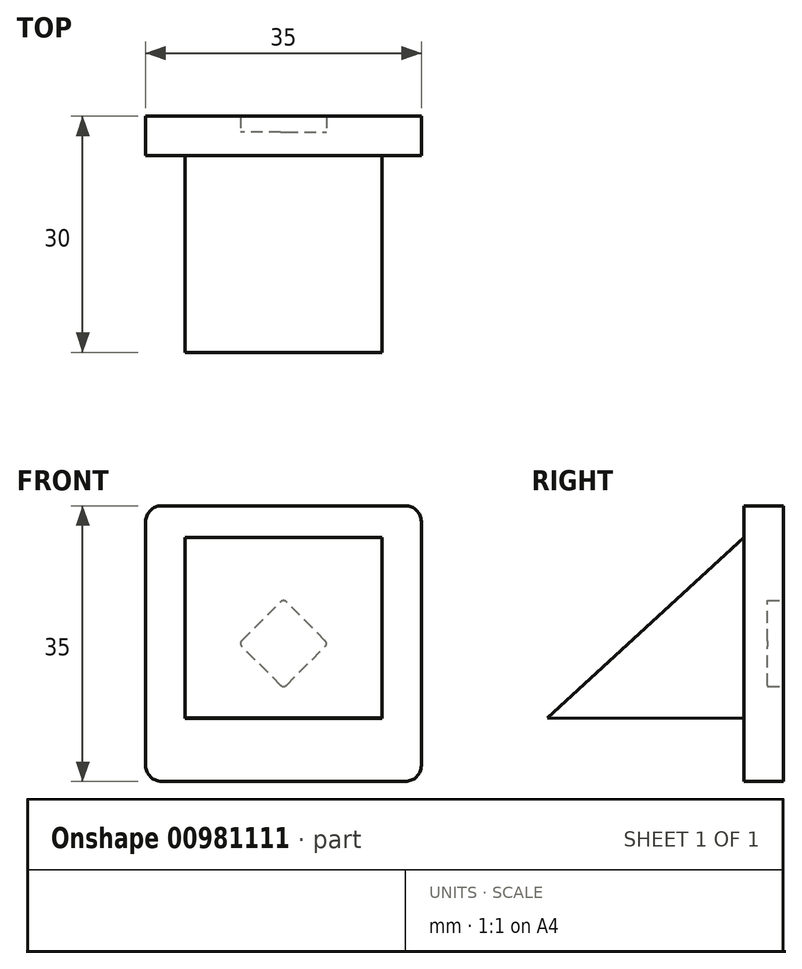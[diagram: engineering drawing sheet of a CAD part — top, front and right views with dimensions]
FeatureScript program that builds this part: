
annotation { "Feature Type Name" : "Feature", "Feature Type Description" : "" }
export const myFeature = defineFeature(function(context is Context, id is Id, definition is map)
    precondition{}
    {
        {
            var Q0;
            Q0=qCreatedBy(makeId("Front.planeOp"),FACE);
            var sketch = newSketch(context, id + "F0", { "sketchPlane" : qUnion([Q0])});
            skLineSegment(sketch, "E0.bottom", {"start": v(-17.5, 35) * mm, "end": v(17.5, 35) * mm});
            skLineSegment(sketch, "E0.top", {"start": v(-17.5, 0) * mm, "end": v(17.5, 0) * mm});
            skLineSegment(sketch, "E0.left", {"start": v(-17.5, 35) * mm, "end": v(-17.5, 0) * mm});
            skLineSegment(sketch, "E0.right", {"start": v(17.5, 35) * mm, "end": v(17.5, 0) * mm});
            skLineSegment(sketch, "E1.bottom", {"start": v(0, 11.84) * mm, "end": v(-5.66, 17.5) * mm});
            skLineSegment(sketch, "E1.top", {"start": v(5.66, 17.5) * mm, "end": v(0, 23.16) * mm});
            skLineSegment(sketch, "E1.left", {"start": v(0, 11.84) * mm, "end": v(5.66, 17.5) * mm});
            skLineSegment(sketch, "E1.right", {"start": v(-5.66, 17.5) * mm, "end": v(0, 23.16) * mm});
            skPoint(sketch, "E1.middle", {"position": v(0, 17.5) * mm});
            skLineSegment(sketch, "E2", {"start": v(-17.5, 17.5) * mm, "end": v(-5.66, 17.5) * mm, "construction": true});
            skArc(sketch, "E3", {"start": v(17.5, 3) * mm, "mid": v(0, 4) * mm, "end": v(-17.5, 3) * mm});
            skLineSegment(sketch, "E4", {"start": v(-17.5, 3) * mm, "end": v(17.5, 3) * mm, "construction": true});
            skSolve(sketch);
        }
        {
            var Q0;
            {var subQ0=sQuery(id+"F0.wireOp",EDGE,"E0.top");Q0=makeQuery(id+"F0.imprint","IMPRINT",FACE,{"disambiguationData":[TD([[makeQuery(id+"F0.imprint","IMPRINT",EDGE,{"derivedFrom":subQ0}),1.0]])]});}
            var Q1;
            {var subQ1=sQuery(id+"F0.wireOp",EDGE,"E0.bottom");Q1=makeQuery(id+"F0.imprint","IMPRINT",FACE,{"disambiguationData":[TD([[makeQuery(id+"F0.imprint","IMPRINT",EDGE,{"derivedFrom":subQ1}),-1.0]])]});}
            var Q2;
            Q2=makeQuery(id+"F0.imprint","IMPRINT",FACE,{"disambiguationData":[TD([[makeQuery(id+"F0.imprint","IMPRINT",EDGE,{"derivedFrom":sQuery(id+"F0.wireOp",EDGE,"E1.bottom")}),-1.0]])]});
            extrude(context, id + "F1", {"entities" : qUnion([Q0, Q1, Q2]), "depth" : 5 * mm, "offsetDistance" : 25 * mm});
        }
        {
            var Q0;
            Q0=makeQuery(id+"F0.imprint","IMPRINT",FACE,{"disambiguationData":[TD([[makeQuery(id+"F0.imprint","IMPRINT",EDGE,{"derivedFrom":sQuery(id+"F0.wireOp",EDGE,"E1.bottom")}),-1.0]])]});
            extrude(context, id + "F2", {"entities" : qUnion([Q0]), "operationType" : NewBodyOperationType.REMOVE, "depth" : 2 * mm, "offsetDistance" : 25 * mm});
        }
        {
            var Q0;
            Q0=makeQuery(id+"F1.opExtrude","SWEPT_EDGE",EDGE,{"disambiguationData":[OSD([sQuery(id+"F0.wireOp",EDGE,"E0.bottom"),sQuery(id+"F0.wireOp",EDGE,"E0.left")])]});
            var Q1;
            Q1=makeQuery(id+"F1.opExtrude","SWEPT_EDGE",EDGE,{"disambiguationData":[OSD([sQuery(id+"F0.wireOp",EDGE,"E0.bottom"),sQuery(id+"F0.wireOp",EDGE,"E0.right")])]});
            var Q2;
            Q2=makeQuery(id+"F1.opExtrude","SWEPT_EDGE",EDGE,{"disambiguationData":[OSD([sQuery(id+"F0.wireOp",EDGE,"E0.top"),sQuery(id+"F0.wireOp",EDGE,"E0.left")])]});
            var Q3;
            Q3=makeQuery(id+"F1.opExtrude","SWEPT_EDGE",EDGE,{"disambiguationData":[OSD([sQuery(id+"F0.wireOp",EDGE,"E0.top"),sQuery(id+"F0.wireOp",EDGE,"E0.right")])]});
            fillet(context, id + "F3", {"entities" : qUnion([Q0, Q1, Q2, Q3]), "radius" : 2 * mm, "tangentPropagation" : true, "allowEdgeOverflow" : false});
        }
        {
            var Q0;
            Q0=makeQuery(id+"F2.boolean.opBoolean","COPY",EDGE,{"derivedFrom":makeQuery(id+"F2.opExtrude","SWEPT_EDGE",EDGE,{"disambiguationData":[OSD([sQuery(id+"F0.wireOp",EDGE,"E1.top"),sQuery(id+"F0.wireOp",EDGE,"E1.left")])]})});
            var Q1;
            Q1=makeQuery(id+"F2.boolean.opBoolean","COPY",EDGE,{"derivedFrom":makeQuery(id+"F2.opExtrude","SWEPT_EDGE",EDGE,{"disambiguationData":[OSD([sQuery(id+"F0.wireOp",EDGE,"E1.top"),sQuery(id+"F0.wireOp",EDGE,"E1.right")])]})});
            var Q2;
            Q2=makeQuery(id+"F2.boolean.opBoolean","COPY",EDGE,{"derivedFrom":makeQuery(id+"F2.opExtrude","SWEPT_EDGE",EDGE,{"disambiguationData":[OSD([sQuery(id+"F0.wireOp",EDGE,"E1.bottom"),sQuery(id+"F0.wireOp",EDGE,"E1.right")])]})});
            var Q3;
            Q3=makeQuery(id+"F2.boolean.opBoolean","COPY",EDGE,{"derivedFrom":makeQuery(id+"F2.opExtrude","SWEPT_EDGE",EDGE,{"disambiguationData":[OSD([sQuery(id+"F0.wireOp",EDGE,"E1.bottom"),sQuery(id+"F0.wireOp",EDGE,"E1.left")])]})});
            fillet(context, id + "F4", {"entities" : qUnion([Q0, Q1, Q2, Q3]), "radius" : .5 * mm, "tangentPropagation" : true, "allowEdgeOverflow" : false});
        }
        {
            var Q0;
            Q0=qCreatedBy(makeId("Right.planeOp"),FACE);
            var sketch = newSketch(context, id + "F5", { "sketchPlane" : qUnion([Q0])});
            skLineSegment(sketch, "E5", {"start": v(-5, 8) * mm, "end": v(-30, 8.05) * mm});
            skLineSegment(sketch, "E6", {"start": v(-30, 8.05) * mm, "end": v(-5, 31) * mm});
            skLineSegment(sketch, "E7", {"start": v(-5, 31) * mm, "end": v(-5, 8) * mm});
            skLineSegment(sketch, "E8", {"start": v(-5, 35) * mm, "end": v(-5, 0) * mm, "construction": true});
            skSolve(sketch);
        }
        {
            var Q0;
            Q0 = qSketchRegion(id + "F5", true);
            extrude(context, id + "F6", {"entities" : qUnion([Q0]), "endBound" : BoundingType.SYMMETRIC, "depth" : 25 * mm, "offsetDistance" : 25 * mm});
        }
    });
